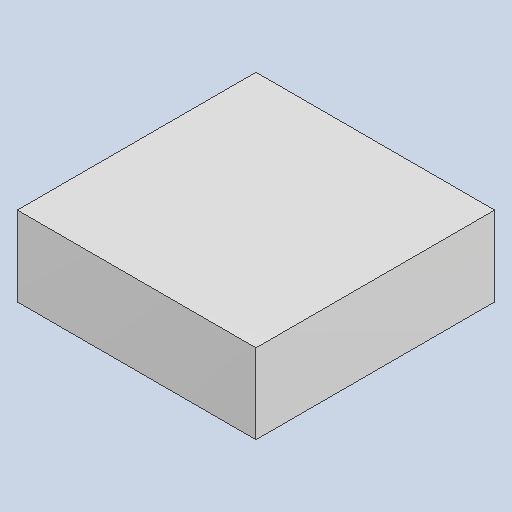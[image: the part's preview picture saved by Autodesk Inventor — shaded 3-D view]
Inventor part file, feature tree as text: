
AUTODESK INVENTOR PART (.ipt)
format: ipt  version: 2023.4 (Build 274418000, 418)  size: 79,872 bytes
history: native  units: mm
features: extrude x1
ambient origin geometry x8: Origin, YZ Plane, XZ Plane, XY Plane, X Axis, Y Axis, Z Axis, Center Point
bodies: Solid1 (feature_tree)
feature tree (1):
  extrude  "Extruded_38"  [1 undecoded]
note: 1 required parameter value undecoded (feature->parameter linkage not recoverable at this tier; creation-order binding heuristic only, values carry confidence <= 0.55)
